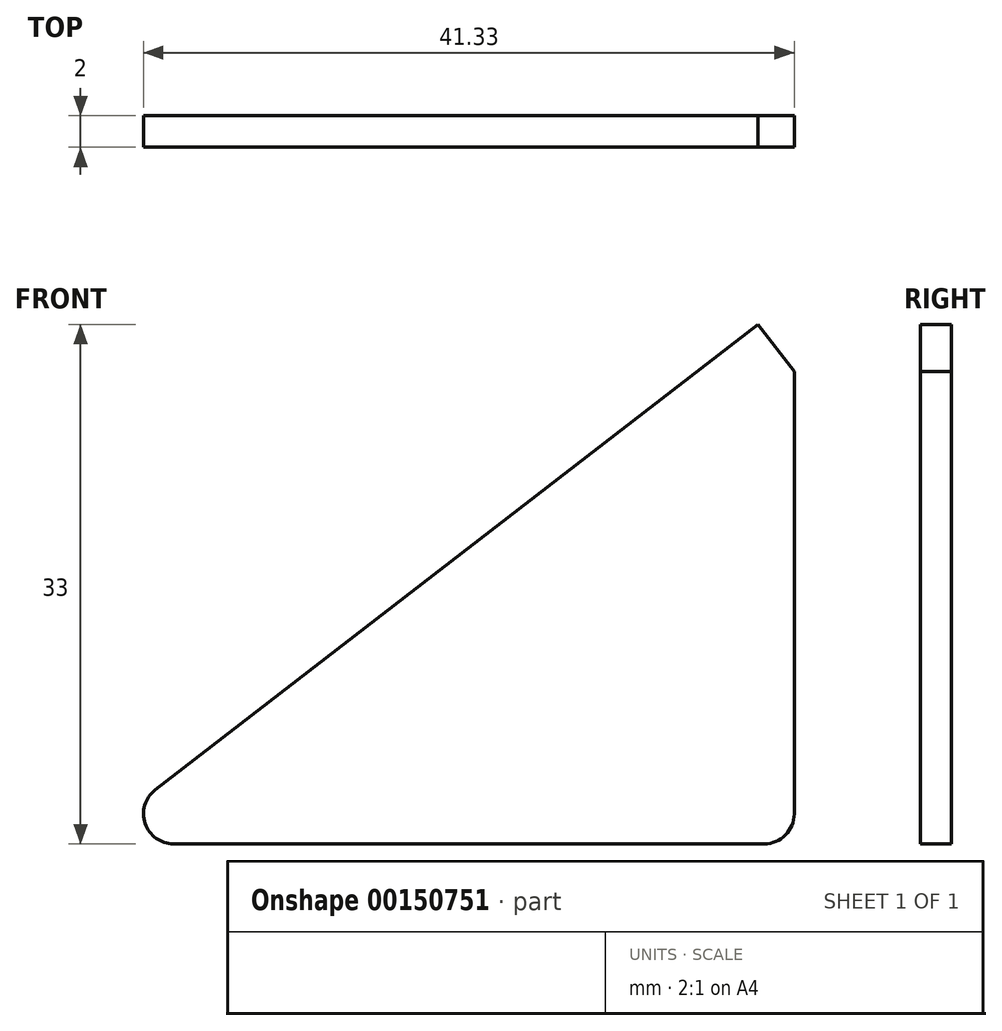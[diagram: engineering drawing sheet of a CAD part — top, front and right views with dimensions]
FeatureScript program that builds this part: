
annotation { "Feature Type Name" : "Feature", "Feature Type Description" : "" }
export const myFeature = defineFeature(function(context is Context, id is Id, definition is map)
    precondition{}
    {
        {
            var Q0;
            Q0=qCreatedBy(makeId("Front.planeOp"),FACE);
            var sketch = newSketch(context, id + "F0", { "sketchPlane" : qUnion([Q0])});
            skLineSegment(sketch, "E0", {"start": v(0, 0) * mm, "end": v(42.68, 33) * mm});
            skLineSegment(sketch, "E1", {"start": v(42.68, 33) * mm, "end": v(45, 30) * mm});
            skLineSegment(sketch, "E2", {"start": v(45, 30) * mm, "end": v(45, 0) * mm});
            skLineSegment(sketch, "E3", {"start": v(0, 0) * mm, "end": v(45, 0) * mm});
            skSolve(sketch);
        }
        {
            var Q0;
            Q0=makeQuery(id+"F0.imprint","IMPRINT",FACE,{"disambiguationData":[TD([[makeQuery(id+"F0.imprint","IMPRINT",EDGE,{"derivedFrom":sQuery(id+"F0.wireOp",EDGE,"E0")}),-1.0]])]});
            extrude(context, id + "F1", {"entities" : qUnion([Q0]), "depth" : 2 * mm});
        }
        {
            var Q0;
            Q0=makeQuery(id+"F1.opExtrude","SWEPT_EDGE",EDGE,{"disambiguationData":[OSD([sQuery(id+"F0.wireOp",EDGE,"E0"),sQuery(id+"F0.wireOp",EDGE,"E3")])]});
            fillet(context, id + "F2", {"entities" : qUnion([Q0]), "radius" : 1.9 * mm, "tangentPropagation" : true, "allowEdgeOverflow" : false});
        }
        {
            var Q0;
            Q0=makeQuery(id+"F1.opExtrude","SWEPT_EDGE",EDGE,{"disambiguationData":[OSD([sQuery(id+"F0.wireOp",EDGE,"E2"),sQuery(id+"F0.wireOp",EDGE,"E3")])]});
            fillet(context, id + "F3", {"entities" : qUnion([Q0]), "radius" : 1.9 * mm, "tangentPropagation" : true, "allowEdgeOverflow" : false});
        }
    });
